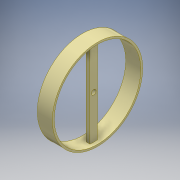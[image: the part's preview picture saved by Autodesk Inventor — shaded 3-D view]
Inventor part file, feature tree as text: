
AUTODESK INVENTOR PART (.ipt)
format: ipt  version: 2016 (Build 200138000, 138)  size: 120,320 bytes
history: native  units: mm
features: extrude x2, sketch x2, other x1
ambient origin geometry x8: Origin, YZ Plane, XZ Plane, XY Plane, X Axis, Y Axis, Z Axis, Center Point
bodies: Body1 (feature_tree)
feature tree (5):
  other  "Sólido1"
  extrude  "Extrusión1"  Depth=4.0mm
  extrude  "Extrusión2"  Depth=23.0mm
  sketch  "Boceto1"  dims[d0=4.0mm d1=46.0mm]
  sketch  "Boceto2"  dims[d2=2.0mm d3=23.0mm d4=2.5mm d5=2.0mm d6=0.0mm d7=48.0mm d8=46.0mm d9=8.0mm d10=0.0mm]
